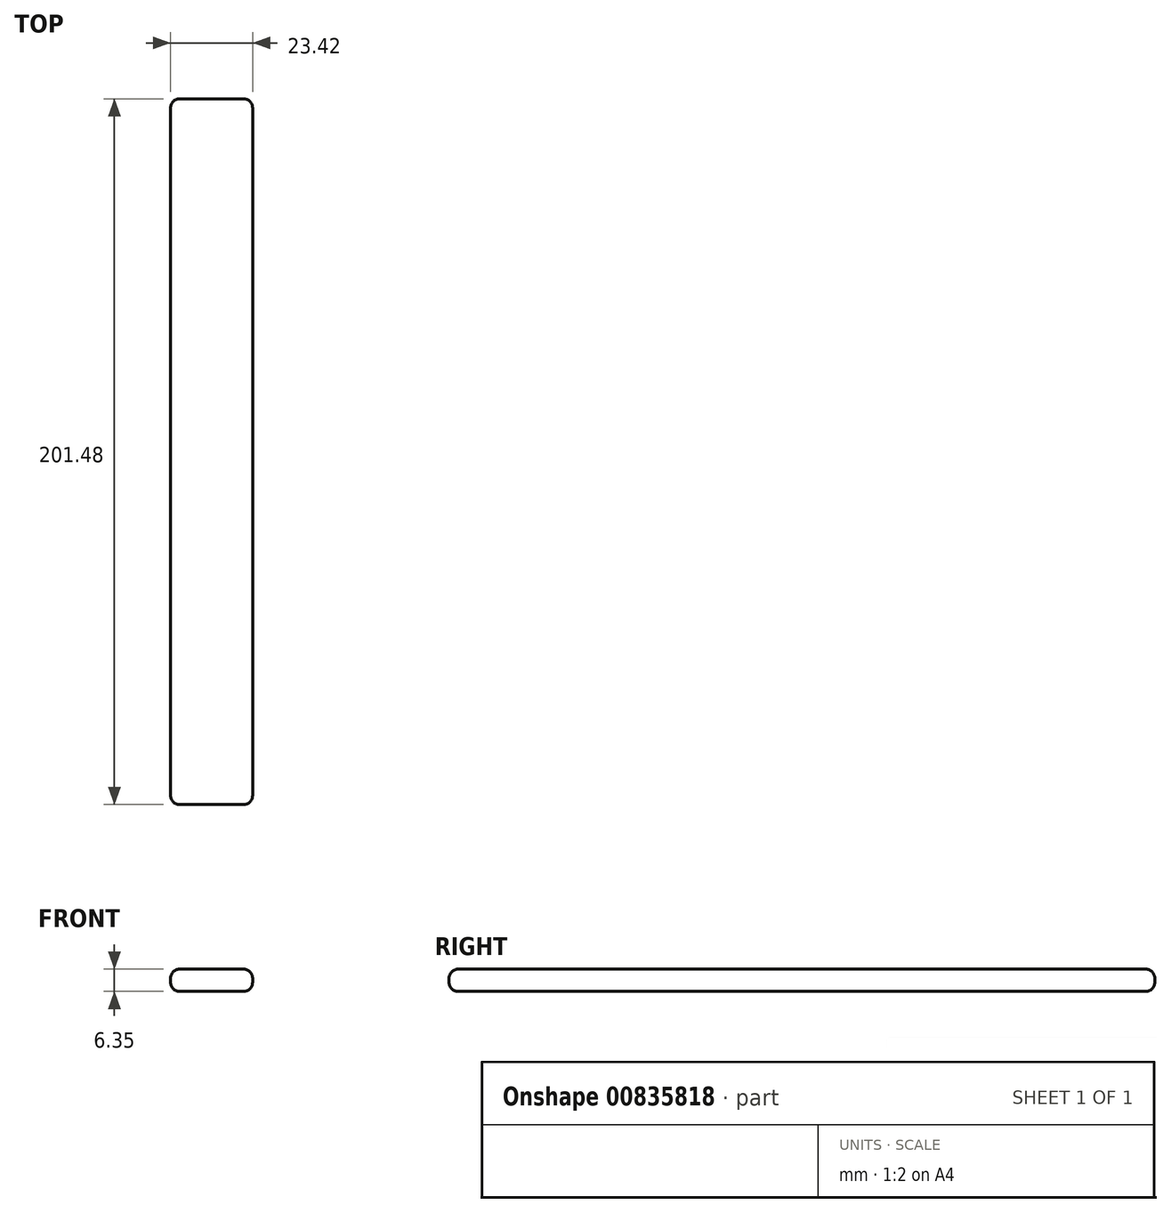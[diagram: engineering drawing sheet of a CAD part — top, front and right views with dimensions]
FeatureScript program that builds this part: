
annotation { "Feature Type Name" : "Feature", "Feature Type Description" : "" }
export const myFeature = defineFeature(function(context is Context, id is Id, definition is map)
    precondition{}
    {
        {
            var Q0;
            Q0=qCreatedBy(makeId("Top.planeOp"),FACE);
            var sketch = newSketch(context, id + "F0", { "sketchPlane" : qUnion([Q0])});
            skText(sketch, "E0", { "text": "I", "fontName": "OpenSans-Regular.ttf"});
            const initialGuessF0  = {"E0": [0, 0, 1, 0, 0.2032]};
            skSetInitialGuess(sketch, initialGuessF0);
            skSolve(sketch);
        }
        {
            var Q0;
            Q0=makeQuery(id+"F0.imprint","IMPRINT",FACE,{"disambiguationData":[TD([[makeQuery(id+"F0.imprint","IMPRINT",EDGE,{"derivedFrom":sQuery(id+"F0.wireOp",EDGE,"E0.sketch_text.stroke-0")}),-1.0]])]});
            extrude(context, id + "F1", {"entities" : qUnion([Q0]), "depth" : 6.35 * mm, "offsetDistance" : 25.4 * mm});
        }
        {
            var Q0;
            Q0=makeQuery(id+"F1.opExtrude","CAP_FACE",FACE,{"disambiguationData":[OSD([sQuery(id+"F0.wireOp",EDGE,"E0.sketch_text.stroke-0"),sQuery(id+"F0.wireOp",EDGE,"E0.sketch_text.stroke-1"),sQuery(id+"F0.wireOp",EDGE,"E0.sketch_text.stroke-2"),sQuery(id+"F0.wireOp",EDGE,"E0.sketch_text.stroke-3")])],"isStart":false});
            var Q1;
            Q1=makeQuery(id+"F1.opExtrude","CAP_FACE",FACE,{"disambiguationData":[OSD([sQuery(id+"F0.wireOp",EDGE,"E0.sketch_text.stroke-0"),sQuery(id+"F0.wireOp",EDGE,"E0.sketch_text.stroke-1"),sQuery(id+"F0.wireOp",EDGE,"E0.sketch_text.stroke-2"),sQuery(id+"F0.wireOp",EDGE,"E0.sketch_text.stroke-3")])],"isStart":true});
            fillet(context, id + "F2", {"entities" : qUnion([Q0, Q1]), "radius" : 2.54 * mm, "tangentPropagation" : true, "allowEdgeOverflow" : false});
        }
        {
            var Q0;
            Q0=makeQuery(id+"F2.opFillet","BLEND_EDGE",EDGE,{"blendedFrom":[makeQuery(id+"F1.opExtrude","CAP_EDGE",EDGE,{"disambiguationData":[OSD([sQuery(id+"F0.wireOp",EDGE,"E0.sketch_text.stroke-2")])],"isStart":false}),makeQuery(id+"F1.opExtrude","CAP_EDGE",EDGE,{"disambiguationData":[OSD([sQuery(id+"F0.wireOp",EDGE,"E0.sketch_text.stroke-3")])],"isStart":false})],"blendedInto":[]});
            var Q1;
            Q1=makeQuery(id+"F1.opExtrude","SWEPT_EDGE",EDGE,{"disambiguationData":[OSD([sQuery(id+"F0.wireOp",EDGE,"E0.sketch_text.stroke-2"),sQuery(id+"F0.wireOp",EDGE,"E0.sketch_text.stroke-3")])]});
            var Q2;
            Q2=makeQuery(id+"F2.opFillet","BLEND_EDGE",EDGE,{"blendedFrom":[makeQuery(id+"F1.opExtrude","CAP_EDGE",EDGE,{"disambiguationData":[OSD([sQuery(id+"F0.wireOp",EDGE,"E0.sketch_text.stroke-2")])],"isStart":true}),makeQuery(id+"F1.opExtrude","CAP_EDGE",EDGE,{"disambiguationData":[OSD([sQuery(id+"F0.wireOp",EDGE,"E0.sketch_text.stroke-3")])],"isStart":true})],"blendedInto":[]});
            var Q3;
            Q3=makeQuery(id+"F2.opFillet","BLEND_EDGE",EDGE,{"blendedFrom":[makeQuery(id+"F1.opExtrude","CAP_EDGE",EDGE,{"disambiguationData":[OSD([sQuery(id+"F0.wireOp",EDGE,"E0.sketch_text.stroke-0")])],"isStart":true}),makeQuery(id+"F1.opExtrude","CAP_EDGE",EDGE,{"disambiguationData":[OSD([sQuery(id+"F0.wireOp",EDGE,"E0.sketch_text.stroke-3")])],"isStart":true})],"blendedInto":[]});
            var Q4;
            Q4=makeQuery(id+"F1.opExtrude","SWEPT_EDGE",EDGE,{"disambiguationData":[OSD([sQuery(id+"F0.wireOp",EDGE,"E0.sketch_text.stroke-0"),sQuery(id+"F0.wireOp",EDGE,"E0.sketch_text.stroke-3")])]});
            var Q5;
            Q5=makeQuery(id+"F2.opFillet","BLEND_EDGE",EDGE,{"blendedFrom":[makeQuery(id+"F1.opExtrude","CAP_EDGE",EDGE,{"disambiguationData":[OSD([sQuery(id+"F0.wireOp",EDGE,"E0.sketch_text.stroke-0")])],"isStart":false}),makeQuery(id+"F1.opExtrude","CAP_EDGE",EDGE,{"disambiguationData":[OSD([sQuery(id+"F0.wireOp",EDGE,"E0.sketch_text.stroke-3")])],"isStart":false})],"blendedInto":[]});
            var Q6;
            Q6=makeQuery(id+"F2.opFillet","BLEND_EDGE",EDGE,{"blendedFrom":[makeQuery(id+"F1.opExtrude","CAP_EDGE",EDGE,{"disambiguationData":[OSD([sQuery(id+"F0.wireOp",EDGE,"E0.sketch_text.stroke-0")])],"isStart":true}),makeQuery(id+"F1.opExtrude","CAP_EDGE",EDGE,{"disambiguationData":[OSD([sQuery(id+"F0.wireOp",EDGE,"E0.sketch_text.stroke-1")])],"isStart":true})],"blendedInto":[]});
            var Q7;
            Q7=makeQuery(id+"F1.opExtrude","SWEPT_EDGE",EDGE,{"disambiguationData":[OSD([sQuery(id+"F0.wireOp",EDGE,"E0.sketch_text.stroke-0"),sQuery(id+"F0.wireOp",EDGE,"E0.sketch_text.stroke-1")])]});
            var Q8;
            Q8=makeQuery(id+"F2.opFillet","BLEND_EDGE",EDGE,{"blendedFrom":[makeQuery(id+"F1.opExtrude","CAP_EDGE",EDGE,{"disambiguationData":[OSD([sQuery(id+"F0.wireOp",EDGE,"E0.sketch_text.stroke-0")])],"isStart":false}),makeQuery(id+"F1.opExtrude","CAP_EDGE",EDGE,{"disambiguationData":[OSD([sQuery(id+"F0.wireOp",EDGE,"E0.sketch_text.stroke-1")])],"isStart":false})],"blendedInto":[]});
            var Q9;
            Q9=makeQuery(id+"F2.opFillet","BLEND_EDGE",EDGE,{"blendedFrom":[makeQuery(id+"F1.opExtrude","CAP_EDGE",EDGE,{"disambiguationData":[OSD([sQuery(id+"F0.wireOp",EDGE,"E0.sketch_text.stroke-1")])],"isStart":true}),makeQuery(id+"F1.opExtrude","CAP_EDGE",EDGE,{"disambiguationData":[OSD([sQuery(id+"F0.wireOp",EDGE,"E0.sketch_text.stroke-2")])],"isStart":true})],"blendedInto":[]});
            var Q10;
            Q10=makeQuery(id+"F1.opExtrude","SWEPT_EDGE",EDGE,{"disambiguationData":[OSD([sQuery(id+"F0.wireOp",EDGE,"E0.sketch_text.stroke-1"),sQuery(id+"F0.wireOp",EDGE,"E0.sketch_text.stroke-2")])]});
            var Q11;
            Q11=makeQuery(id+"F2.opFillet","BLEND_EDGE",EDGE,{"blendedFrom":[makeQuery(id+"F1.opExtrude","CAP_EDGE",EDGE,{"disambiguationData":[OSD([sQuery(id+"F0.wireOp",EDGE,"E0.sketch_text.stroke-1")])],"isStart":false}),makeQuery(id+"F1.opExtrude","CAP_EDGE",EDGE,{"disambiguationData":[OSD([sQuery(id+"F0.wireOp",EDGE,"E0.sketch_text.stroke-2")])],"isStart":false})],"blendedInto":[]});
            fillet(context, id + "F3", {"entities" : qUnion([Q0, Q1, Q2, Q3, Q4, Q5, Q6, Q7, Q8, Q9, Q10, Q11]), "radius" : 2.54 * mm, "tangentPropagation" : true, "allowEdgeOverflow" : false});
        }
    });
